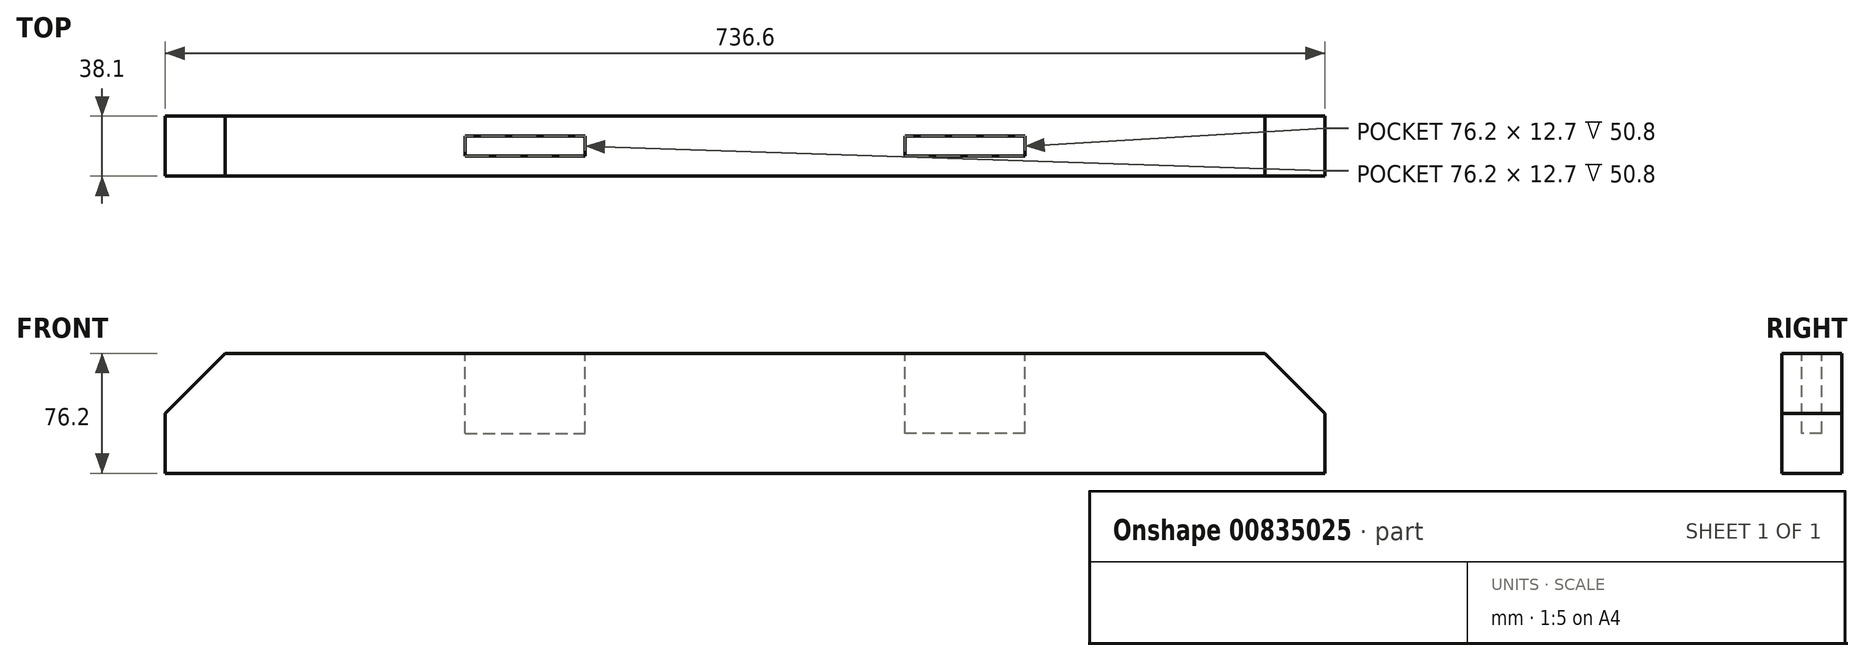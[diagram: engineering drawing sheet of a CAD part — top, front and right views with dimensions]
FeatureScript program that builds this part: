
annotation { "Feature Type Name" : "Feature", "Feature Type Description" : "" }
export const myFeature = defineFeature(function(context is Context, id is Id, definition is map)
    precondition{}
    {
        {
            var Q0;
            Q0=qCreatedBy(makeId("Front.planeOp"),FACE);
            var sketch = newSketch(context, id + "F0", { "sketchPlane" : qUnion([Q0])});
            skLineSegment(sketch, "E0.bottom", {"start": v(-368.3, 0) * mm, "end": v(368.3, 0) * mm});
            skLineSegment(sketch, "E0.top", {"start": v(-368.3, 76.2) * mm, "end": v(368.3, 76.2) * mm});
            skLineSegment(sketch, "E0.left", {"start": v(-368.3, 0) * mm, "end": v(-368.3, 76.2) * mm});
            skLineSegment(sketch, "E0.right", {"start": v(368.3, 0) * mm, "end": v(368.3, 76.2) * mm});
            skSolve(sketch);
        }
        {
            var Q0;
            Q0 = qSketchRegion(id + "F0", true);
            extrude(context, id + "F1", {"entities" : qUnion([Q0]), "depth" : 38.1 * mm, "offsetDistance" : 25.4 * mm});
        }
        {
            var Q0;
            Q0=makeQuery(id+"F1.opExtrude","SWEPT_EDGE",EDGE,{"disambiguationData":[OSD([sQuery(id+"F0.wireOp",EDGE,"E0.top"),sQuery(id+"F0.wireOp",EDGE,"E0.left")])]});
            var Q1;
            Q1=makeQuery(id+"F1.opExtrude","SWEPT_EDGE",EDGE,{"disambiguationData":[OSD([sQuery(id+"F0.wireOp",EDGE,"E0.top"),sQuery(id+"F0.wireOp",EDGE,"E0.right")])]});
            chamfer(context, id + "F2", {"entities" : qUnion([Q0, Q1]), "width" : 38.1 * mm, "tangentPropagation" : true});
        }
        {
            var Q0;
            Q0=makeQuery(id+"F1.opExtrude","SWEPT_FACE",FACE,{"disambiguationData":[OSD([sQuery(id+"F0.wireOp",EDGE,"E0.top")])]});
            var sketch = newSketch(context, id + "F3", { "sketchPlane" : qUnion([Q0])});
            skLineSegment(sketch, "E1.bottom", {"start": v(-177.8, -12.7) * mm, "end": v(-101.6, -12.7) * mm});
            skLineSegment(sketch, "E1.top", {"start": v(-177.8, -25.4) * mm, "end": v(-101.6, -25.4) * mm});
            skLineSegment(sketch, "E1.left", {"start": v(-177.8, -12.7) * mm, "end": v(-177.8, -25.4) * mm});
            skLineSegment(sketch, "E1.right", {"start": v(-101.6, -12.7) * mm, "end": v(-101.6, -25.4) * mm});
            skPoint(sketch, "E2", {"position": v(-101.6, -19.05) * mm});
            skLineSegment(sketch, "E3.MirrorCS", {"start": v(101.6, -12.7) * mm, "end": v(101.6, -25.4) * mm});
            skLineSegment(sketch, "E4.MirrorCS", {"start": v(177.8, -12.7) * mm, "end": v(177.8, -25.4) * mm});
            skLineSegment(sketch, "E5.MirrorCS", {"start": v(177.8, -25.4) * mm, "end": v(101.6, -25.4) * mm});
            skLineSegment(sketch, "E6.MirrorCS", {"start": v(177.8, -12.7) * mm, "end": v(101.6, -12.7) * mm});
            skSolve(sketch);
        }
        {
            var Q0;
            Q0 = qSketchRegion(id + "F3", true);
            extrude(context, id + "F4", {"entities" : qUnion([Q0]), "operationType" : NewBodyOperationType.REMOVE, "oppositeDirection" : true, "depth" : 50.8 * mm, "offsetDistance" : 25.4 * mm});
        }
    });
